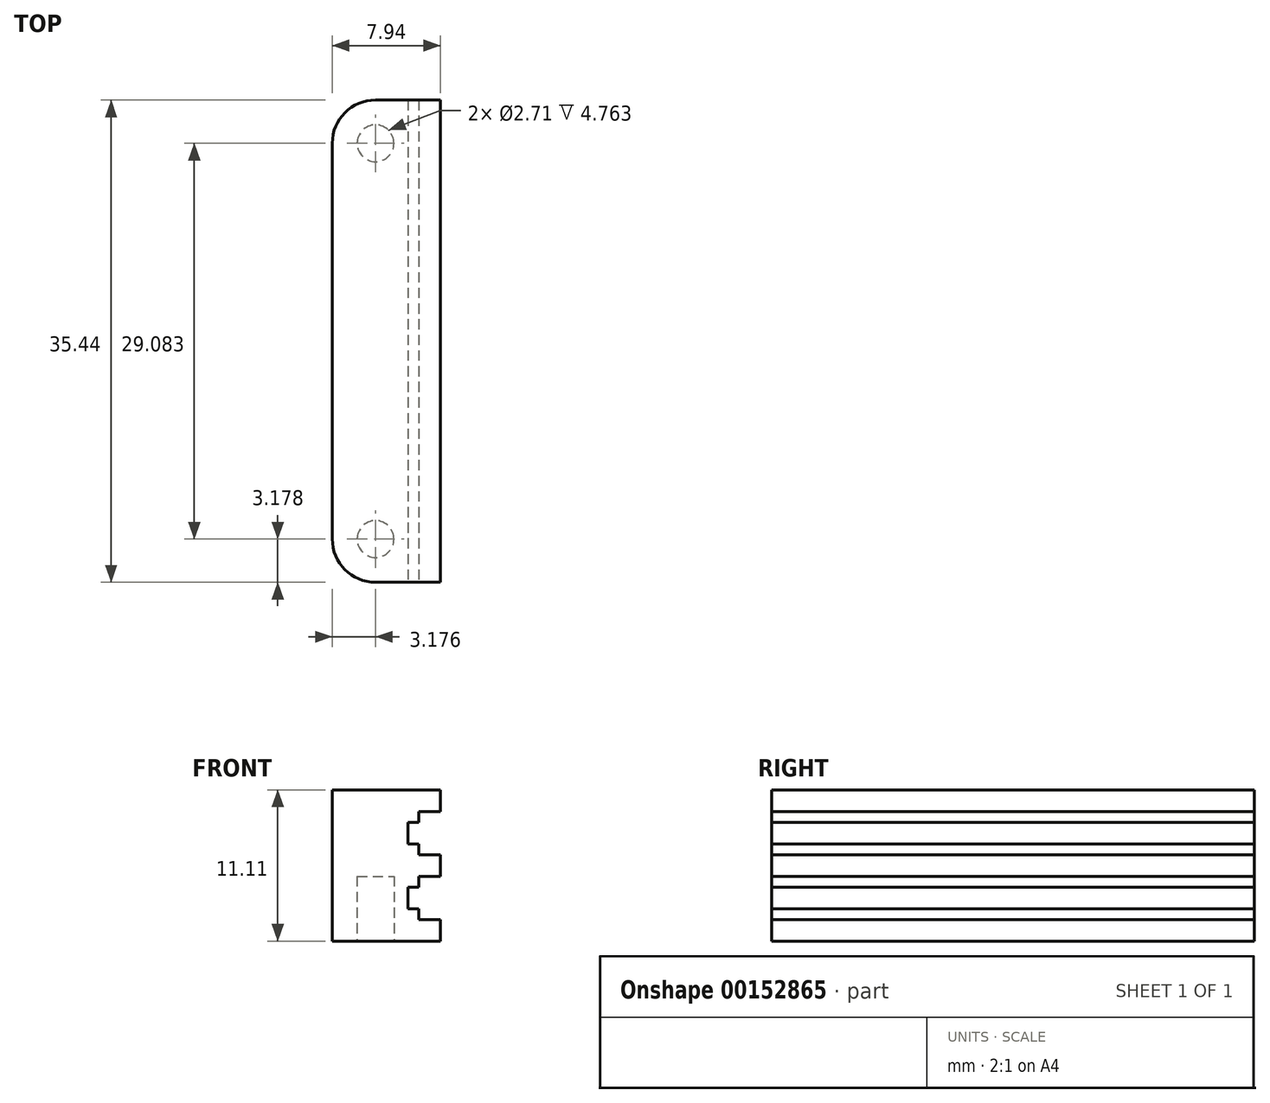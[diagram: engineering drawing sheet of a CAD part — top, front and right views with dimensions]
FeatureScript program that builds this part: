
annotation { "Feature Type Name" : "Feature", "Feature Type Description" : "" }
export const myFeature = defineFeature(function(context is Context, id is Id, definition is map)
    precondition{}
    {
        {
            var Q0;
            Q0=qCreatedBy(makeId("Top.planeOp"),FACE);
            var sketch = newSketch(context, id + "F0", { "sketchPlane" : qUnion([Q0])});
            skLineSegment(sketch, "E0.bottom", {"start": v(3.97, -17.72) * mm, "end": v(-3.97, -17.72) * mm});
            skLineSegment(sketch, "E0.top", {"start": v(3.97, 17.72) * mm, "end": v(-3.97, 17.72) * mm});
            skLineSegment(sketch, "E0.left", {"start": v(3.97, -17.72) * mm, "end": v(3.97, 17.72) * mm});
            skLineSegment(sketch, "E0.right", {"start": v(-3.97, -17.72) * mm, "end": v(-3.97, 17.72) * mm});
            skPoint(sketch, "E0.middle", {"position": v(0, 0) * mm});
            skSolve(sketch);
        }
        {
            var Q0;
            Q0=makeQuery(id+"F0.imprint","IMPRINT",FACE,{"disambiguationData":[TD([[makeQuery(id+"F0.imprint","IMPRINT",EDGE,{"derivedFrom":sQuery(id+"F0.wireOp",EDGE,"E0.bottom")}),-1.0]])]});
            extrude(context, id + "F1", {"entities" : qUnion([Q0]), "depth" : 11.1 * mm});
        }
        {
            var Q0;
            Q0=makeQuery(id+"F1.opExtrude","SWEPT_FACE",FACE,{"disambiguationData":[OSD([sQuery(id+"F0.wireOp",EDGE,"E0.bottom")])]});
            var sketch = newSketch(context, id + "F2", { "sketchPlane" : qUnion([Q0])});
            skLineSegment(sketch, "E1.bottom", {"start": v(2.38, 9.52) * mm, "end": v(3.97, 9.52) * mm});
            skLineSegment(sketch, "E1.top", {"start": v(2.38, 6.35) * mm, "end": v(3.97, 6.35) * mm});
            skLineSegment(sketch, "E1.right", {"start": v(3.97, 9.52) * mm, "end": v(3.97, 6.35) * mm});
            skLineSegment(sketch, "E2", {"start": v(2.38, 6.35) * mm, "end": v(2.38, 4.76) * mm, "construction": true});
            skLineSegment(sketch, "E3.bottom", {"start": v(2.38, 4.76) * mm, "end": v(3.97, 4.76) * mm});
            skLineSegment(sketch, "E3.top", {"start": v(2.38, 1.59) * mm, "end": v(3.97, 1.59) * mm});
            skLineSegment(sketch, "E3.right", {"start": v(3.97, 4.76) * mm, "end": v(3.97, 1.59) * mm});
            skLineSegment(sketch, "E4", {"start": v(2.38, 9.53) * mm, "end": v(2.38, 8.73) * mm});
            skLineSegment(sketch, "E5", {"start": v(2.38, 6.35) * mm, "end": v(2.38, 7.14) * mm});
            skLineSegment(sketch, "E6.bottom", {"start": v(2.38, 8.73) * mm, "end": v(1.59, 8.73) * mm});
            skLineSegment(sketch, "E6.top", {"start": v(2.38, 7.14) * mm, "end": v(1.59, 7.14) * mm});
            skLineSegment(sketch, "E6.left", {"start": v(2.38, 8.73) * mm, "end": v(2.38, 7.14) * mm, "construction": true});
            skLineSegment(sketch, "E6.right", {"start": v(1.59, 8.73) * mm, "end": v(1.59, 7.14) * mm});
            skLineSegment(sketch, "E7", {"start": v(2.38, 1.59) * mm, "end": v(2.38, 2.38) * mm});
            skLineSegment(sketch, "E8", {"start": v(2.38, 4.76) * mm, "end": v(2.38, 3.97) * mm});
            skLineSegment(sketch, "E9.bottom", {"start": v(2.38, 3.97) * mm, "end": v(1.59, 3.97) * mm});
            skLineSegment(sketch, "E9.top", {"start": v(2.38, 2.38) * mm, "end": v(1.59, 2.38) * mm});
            skLineSegment(sketch, "E9.left", {"start": v(2.38, 3.97) * mm, "end": v(2.38, 2.38) * mm, "construction": true});
            skLineSegment(sketch, "E9.right", {"start": v(1.59, 3.97) * mm, "end": v(1.59, 2.38) * mm});
            skSolve(sketch);
        }
        {
            var Q0;
            Q0=qSketchRegion(id+"F2",true);
            var Q1;
            Q1=makeQuery(id+"F1.opExtrude","SWEPT_FACE",FACE,{"disambiguationData":[OSD([sQuery(id+"F0.wireOp",EDGE,"E0.top")])]});
            extrude(context, id + "F3", {"entities" : qUnion([Q0]), "operationType" : NewBodyOperationType.REMOVE, "endBound" : BoundingType.UP_TO_SURFACE, "oppositeDirection" : true, "endBoundEntityFace" : qUnion([Q1]), "depth" : 25.4 * mm});
        }
        {
            var Q0;
            Q0=makeQuery(id+"F1.opExtrude","CAP_FACE",FACE,{"disambiguationData":[OSD([sQuery(id+"F0.wireOp",EDGE,"E0.bottom"),sQuery(id+"F0.wireOp",EDGE,"E0.top"),sQuery(id+"F0.wireOp",EDGE,"E0.left"),sQuery(id+"F0.wireOp",EDGE,"E0.right")])],"isStart":true});
            var sketch = newSketch(context, id + "F4", { "sketchPlane" : qUnion([Q0])});
            skLineSegment(sketch, "E10", {"start": v(-0.8, 17.72) * mm, "end": v(-0.8, 14.54) * mm, "construction": true});
            skLineSegment(sketch, "E11", {"start": v(-0.8, -17.72) * mm, "end": v(-0.8, -14.54) * mm, "construction": true});
            skCircle(sketch, "E12", {"center": v(-0.8, 14.54) * mm, "radius": 1.35 * mm});
            skCircle(sketch, "E13", {"center": v(-0.8, -14.54) * mm, "radius": 1.35 * mm});
            skLineSegment(sketch, "E14", {"start": v(-0.8, 14.54) * mm, "end": v(-0.8, -14.54) * mm, "construction": true});
            skLineSegment(sketch, "E15", {"start": v(-3.97, 0) * mm, "end": v(-0.8, 0) * mm, "construction": true});
            skSolve(sketch);
        }
        {
            var Q0;
            Q0 = qSketchRegion(id + "F4", true);
            extrude(context, id + "F5", {"entities" : qUnion([Q0]), "operationType" : NewBodyOperationType.REMOVE, "oppositeDirection" : true, "depth" : 4.76 * mm});
        }
        {
            var Q0;
            Q0=makeQuery(id+"F1.opExtrude","SWEPT_EDGE",EDGE,{"disambiguationData":[OSD([sQuery(id+"F0.wireOp",EDGE,"E0.top"),sQuery(id+"F0.wireOp",EDGE,"E0.right")])]});
            var Q1;
            Q1=makeQuery(id+"F1.opExtrude","SWEPT_EDGE",EDGE,{"disambiguationData":[OSD([sQuery(id+"F0.wireOp",EDGE,"E0.bottom"),sQuery(id+"F0.wireOp",EDGE,"E0.right")])]});
            fillet(context, id + "F6", {"entities" : qUnion([Q0, Q1]), "radius" : 3.17 * mm, "tangentPropagation" : true, "allowEdgeOverflow" : false});
        }
    });
